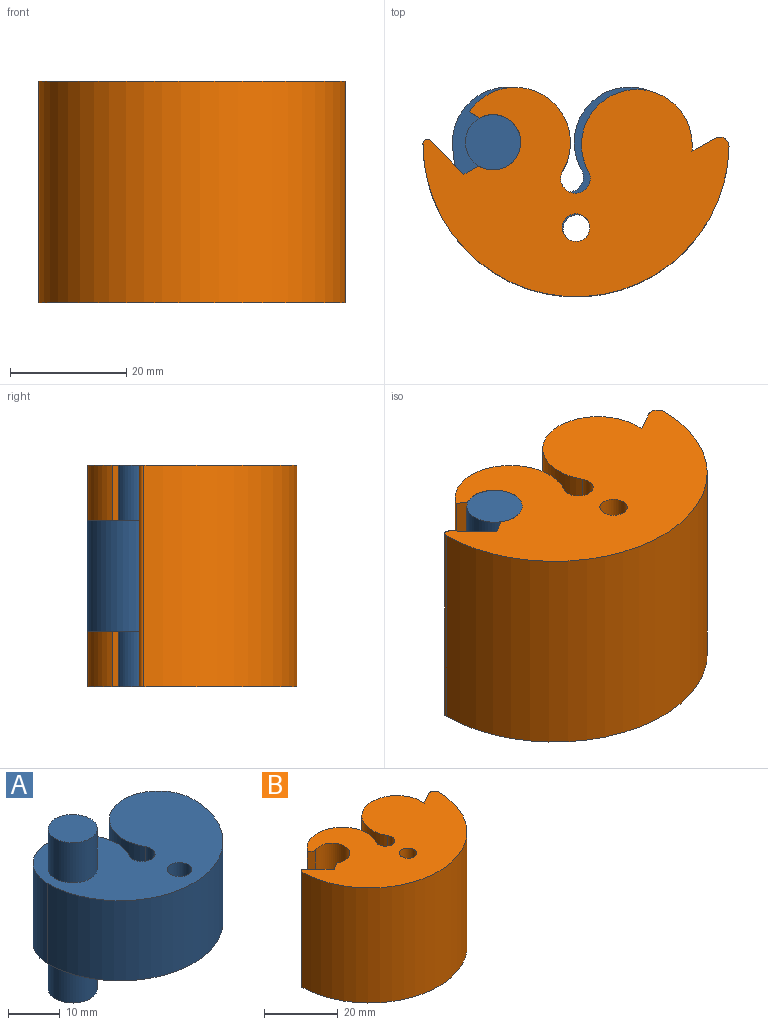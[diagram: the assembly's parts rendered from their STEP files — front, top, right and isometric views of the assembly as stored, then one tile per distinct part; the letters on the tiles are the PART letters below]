
ASSEMBLY  parts=2 mates=1
PART A: 11 faces, bbox 40x29.5x38.1 mm
  f0: cylinder r=9.53mm len=19.05mm, axis (0,0,-1), area 664.2mm2, adj f1,f3,f4,f5
  f1: cylinder r=20mm len=40.01mm, axis (0,0,-1), area 1197.1mm2, adj f0,f2,f4,f5
  f2: cylinder r=9.53mm len=19.05mm, axis (0,0,-1), area 664.2mm2, adj f1,f3,f4,f5
  f3: cylinder r=2.54mm len=19.05mm, axis (0,0,-1), area 202.2mm2, adj f0,f2,f4,f5
  f4: plane 40.01x29.53mm, normal (0,0,1), area 795.3mm2, adj f0,f1,f2,f3,f8,f10
  f5: plane 40.01x29.53mm, normal (0,0,-1), area 795.3mm2, adj f0,f1,f2,f3,f7,f10
  f6: plane 9.53x9.53mm, normal (0,0,-1), area 71.3mm2, adj f7
  f7: cylinder r=4.76mm len=9.53mm, axis (0,0,-1), area 285mm2, adj f5,f6
  f8: cylinder r=4.76mm len=9.53mm, axis (0,0,-1), area 285mm2, adj f4,f9
  f9: plane 9.53x9.53mm, normal (0,0,1), area 71.3mm2, adj f8
  f10: cylinder r=2.38mm len=19.05mm, axis (0,0,1), area 285mm2, adj f4,f5
PART B: 26 faces, bbox 52.7x35.9x38.1 mm
  f0: cylinder r=20mm len=9.53mm, axis (0,0,-1), area 8.9mm2, adj f3,f7,f8,f23
  f1: cylinder r=4.76mm len=9.53mm, axis (0,0,-1), area 189.9mm2, adj f2,f6,f7,f8
  f2: plane 9.53x2.54mm, normal (-0.5,0.87,0), area 27.9mm2, adj f1,f7,f8,f19
  f3: cylinder r=9.53mm len=19.05mm, axis (0,0,-1), area 332.1mm2, adj f0,f4,f7,f8
  f4: cylinder r=2.54mm len=9.53mm, axis (0,0,-1), area 101.1mm2, adj f3,f5,f7,f8
  f5: cylinder r=9.53mm len=17.52mm, axis (0,0,-1), area 280mm2, adj f4,f6,f7,f8
  f6: plane 9.53x1.81mm, normal (-0.5,-0.87,0), area 19.9mm2, adj f1,f5,f7,f8
  f7: plane 52.7x35.88mm, normal (0,0,1), area 1234mm2, adj f0,f1,f2,f3,f4,f5,f6,f19
  f8: plane 39.21x29.53mm, normal (0,0,-1), area 780.2mm2, adj f0,f1,f2,f3,f4,f5,f6,f9
  f9: cylinder r=20mm len=39.19mm, axis (0,0,1), area 1071.4mm2, adj f8,f18,f19,f23
  f10: cylinder r=20mm len=9.53mm, axis (0,0,1), area 8.9mm2, adj f13,f17,f18,f23
  f11: cylinder r=4.76mm len=9.53mm, axis (0,0,1), area 189.9mm2, adj f12,f16,f17,f18
  f12: plane 9.53x2.54mm, normal (-0.5,0.87,0), area 27.9mm2, adj f11,f17,f18,f19
  f13: cylinder r=9.53mm len=19.05mm, axis (0,0,1), area 332.1mm2, adj f10,f14,f17,f18
  f14: cylinder r=2.54mm len=9.53mm, axis (0,0,1), area 101.1mm2, adj f13,f15,f17,f18
  f15: cylinder r=9.53mm len=17.52mm, axis (0,0,1), area 280mm2, adj f14,f16,f17,f18
  f16: plane 9.53x1.81mm, normal (-0.5,-0.87,0), area 19.9mm2, adj f11,f15,f17,f18
  f17: plane 52.7x35.88mm, normal (0,0,-1), area 1234mm2, adj f10,f11,f12,f13,f14,f15,f16,f19
  f18: plane 39.21x29.53mm, normal (0,0,1), area 780.2mm2, adj f9,f10,f11,f12,f13,f14,f15,f16
  f19: plane 38.1x5.79mm, normal (0.7,0.71,0), area 309.9mm2, adj f2,f7,f9,f12,f17,f20
  f20: cylinder r=0.79mm len=38.1mm, axis (0,0,1), area 71.6mm2, adj f7,f17,f19,f21
  f21: cylinder r=26.35mm len=52.7mm, axis (0,0,1), area 3136.5mm2, adj f7,f17,f20,f22
  f22: cylinder r=1.59mm len=38.1mm, axis (0,0,1), area 126.7mm2, adj f7,f17,f21,f23
  f23: plane 38.1x3.99mm, normal (-0.5,0.87,0), area 175.6mm2, adj f0,f7,f9,f10,f17,f22
  f24: cylinder r=2.38mm len=9.53mm, axis (0,0,1), area 142.5mm2, adj f17,f18
  f25: cylinder r=2.38mm len=9.53mm, axis (0,0,1), area 142.5mm2, adj f7,f8
PLACE A t=(-3.81,-21.11,0)mm fixed
PLACE B rot(axis=(0,0,-1),1deg) t=(-78.73,-20.03,0)mm
MATE revolute B.f1 <-> A.f7  axis (0,0,1) through (-16.82,-21.11,19.05)mm
